# Revit family: Электронная проходная PERCo_КТО2.9
name_source: partatom
category: Оборудование
units: mm (PartAtom-declared; Revit-internal decimal feet)

## family parameters
Всегда вертикально = Нет
Классификация = Нет
На основе рабочей плоскости = Нет
Общий = Нет
При загрузке вырезать с полостями = Нет
Размер круглого соединителя = Использовать диаметр
Тип детали = Нормальный
Точка расчета площади = Нет

## types (3) — shared parameters
ADSK_URL страницы изделия = https://www.perco.ru
ADSK_Единица измерения = шт.
ADSK_Завод-изготовитель = PERCo
ADSK_Количество = 1
ADSK_Масса_Текст = не более 35 кг
ADSK_Материал наименование = Крышка стойки турникета и планки выполнены из высококачественной нержавеющей стали. Стойка турникета – сталь, покрытая порошковой краской.
ADSK_Напряжение = 12 В
ADSK_Номинальная мощность = 10 Вт
ADSK_Ток = 1 А
Габаритные размеры (длина×ширина×высота) = 640×683×1084 мм
Длина планки = 465 мм
Емкость картоприемника = Не предусмотрено
Корпус = PERCo_Нержавейка
Панель = PERCo_Пластик черный
Подключение к электросети = 220 В
Пропускная способность = 30 чел./мин
Степень защиты оболочки = IP41
Температура использования = от +1°С до +50°С
Тип планки "Антипаника" = Механическая
Формат читаемых карт = Mifare, EMM, HID Prox
Ширина зоны прохода = 500 мм.

## per-type parameters (varying)
| type | ADSK_Наименование | ADSK_Наименование краткое | Наличие сканеров отпечатка пальцев | Наличие сканеров штрих-кода | Сканер отпечатка пальцев | Сканер штрих-кода | Тип контроллера |
| КТ02.9Q | Электронная проходная PERCo-KT02.9Q со встроенными сканерами штрихкода | Электронная проходная KT02.9Q | Нет | Да | Нет | Да | CT13 |
| КТ02.9 | Электронная проходная PERCo-KT02.9 для карт EMM/HID, Mifare стандарта ISO 14443 с опцией защиты от копирования, смартфонов | Электронная проходная KT02.9 | Нет | Нет | Нет | Нет | CT03.2 |
| КТ02.9B | Электронная проходная PERCo-KT02.9B со встроенными сканерами отпечатков пальцев | Электронная проходная KT02.9B | Да | Нет | Да | Нет | CT13 |
